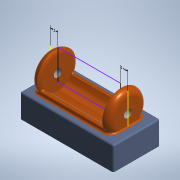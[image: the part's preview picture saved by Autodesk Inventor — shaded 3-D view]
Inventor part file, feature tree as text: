
AUTODESK INVENTOR PART (.ipt)
format: ipt  version: 2022 (Build 260153000, 153)  size: 436,736 bytes
history: native  units: mm (DEFAULTED — no unit token found)
features: sketch x6, extrude x5, fillet x4, plane x1
ambient origin geometry x8: Origin, YZ Plane, XZ Plane, XY Plane, X Axis, Y Axis, Z Axis, Center Point
bodies: Solid1 (feature_tree)
feature tree (16):
  extrude  "Extrusion1"  Depth=100.0mm TaperAngle=0.0deg
  plane  "Work Plane1"
  extrude  "Extrusion2"  Depth=120.0mm
  sketch  "Sketch3"  dims[d5=60.0mm d6=30.0mm d7=0.0mm]
  extrude  "Extrusion3"  Depth=30.0mm TaperAngle=0.0deg
  extrude  "Extrusion4"  Depth=10.0mm
  fillet  "Fillet1"  Radius=50.0mm
  fillet  "Fillet2"  Radius=10.0mm
  fillet  "Fillet3"  Radius=50.0mm
  extrude  "Extrusion5"  Depth=8.0mm
  fillet  "Fillet4"  Radius=2.0mm
  sketch  "Sketch1"  dims[d0=50.0mm d1=100.0mm d2=0.0mm]
  sketch  "Sketch2"  dims[d3=-14.5mm d4=120.0mm]
  sketch  "Sketch4"  dims[d8=10.0mm d9=10.0mm d10=50.0mm d11=0.0mm d12=10.0mm d13=50.0mm d14=0.0mm]
  sketch  "Sketch5"  dims[d15=2.0mm d16=8.0mm d17=2.0mm]
  sketch  "Sketch6"  dims[d18=2.0mm d19=10.0mm d20=0.0mm d21=2.0mm]
